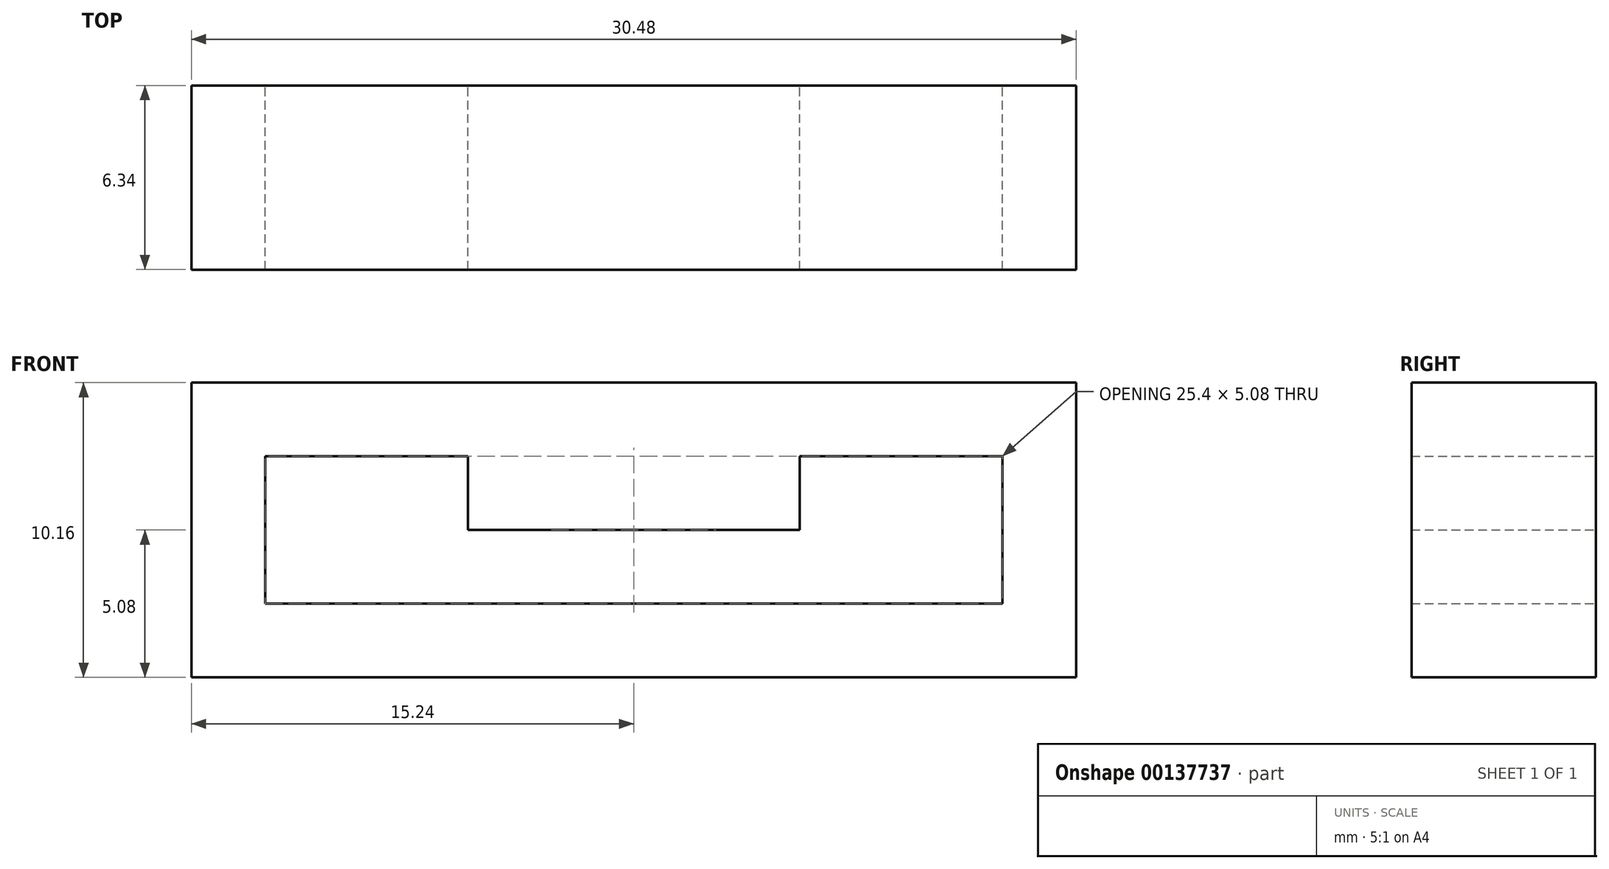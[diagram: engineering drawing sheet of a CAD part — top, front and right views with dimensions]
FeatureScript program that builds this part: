
annotation { "Feature Type Name" : "Feature", "Feature Type Description" : "" }
export const myFeature = defineFeature(function(context is Context, id is Id, definition is map)
    precondition{}
    {
        {
            var Q0;
            Q0=qCreatedBy(makeId("Front.planeOp"),FACE);
            var sketch = newSketch(context, id + "F0", { "sketchPlane" : qUnion([Q0])});
            skLineSegment(sketch, "E0.bottom", {"start": v(15.24, 5.08) * mm, "end": v(-15.24, 5.08) * mm});
            skLineSegment(sketch, "E0.top", {"start": v(15.24, -5.08) * mm, "end": v(-15.24, -5.08) * mm});
            skLineSegment(sketch, "E0.left", {"start": v(15.24, 5.08) * mm, "end": v(15.24, -5.08) * mm});
            skLineSegment(sketch, "E0.right", {"start": v(-15.24, 5.08) * mm, "end": v(-15.24, -5.08) * mm});
            skPoint(sketch, "E0.middle", {"position": v(0, 0) * mm});
            skLineSegment(sketch, "E1.bottom", {"start": v(12.7, 2.54) * mm, "end": v(-12.7, 2.54) * mm});
            skLineSegment(sketch, "E1.top", {"start": v(12.7, -2.54) * mm, "end": v(-12.7, -2.54) * mm});
            skLineSegment(sketch, "E1.left", {"start": v(12.7, 2.54) * mm, "end": v(12.7, -2.54) * mm});
            skLineSegment(sketch, "E1.right", {"start": v(-12.7, 2.54) * mm, "end": v(-12.7, -2.54) * mm});
            skLineSegment(sketch, "E2.bottom", {"start": v(-10.86, 5.08) * mm, "end": v(10.73, 5.08) * mm});
            skLineSegment(sketch, "E2.top", {"start": v(-10.86, 2.54) * mm, "end": v(10.73, 2.54) * mm});
            skLineSegment(sketch, "E2.left", {"start": v(-10.86, 5.08) * mm, "end": v(-10.86, 2.54) * mm});
            skLineSegment(sketch, "E2.right", {"start": v(10.73, 5.08) * mm, "end": v(10.73, 2.54) * mm});
            skSolve(sketch);
        }
        {
            var Q0;
            Q0 = qSketchRegion(id + "F0", true);
            extrude(context, id + "F1", {"entities" : qUnion([Q0]), "endBound" : BoundingType.SYMMETRIC, "depth" : 6.35 * mm});
        }
        {
            var Q0;
            Q0=makeQuery(id+"F1.opExtrude","SWEPT_FACE",FACE,{"disambiguationData":[OSD([sQuery(id+"F0.wireOp",EDGE,"E1.bottom"),sQuery(id+"F0.wireOp",EDGE,"E2.top")])]});
            var sketch = newSketch(context, id + "F2", { "sketchPlane" : qUnion([Q0])});
            skLineSegment(sketch, "E3.bottom", {"start": v(5.72, 3.18) * mm, "end": v(-5.72, 3.18) * mm});
            skLineSegment(sketch, "E3.top", {"start": v(5.72, -3.18) * mm, "end": v(-5.72, -3.18) * mm});
            skLineSegment(sketch, "E3.left", {"start": v(5.72, 3.18) * mm, "end": v(5.72, -3.18) * mm});
            skLineSegment(sketch, "E3.right", {"start": v(-5.72, 3.18) * mm, "end": v(-5.72, -3.18) * mm});
            skPoint(sketch, "E3.middle", {"position": v(0, 0) * mm});
            skSolve(sketch);
        }
        {
            var Q0;
            Q0=makeQuery(id+"F2.imprint","IMPRINT",FACE,{"disambiguationData":[TD([[makeQuery(id+"F2.imprint","IMPRINT",EDGE,{"derivedFrom":sQuery(id+"F2.wireOp",EDGE,"E3.bottom")}),1.0]])]});
            extrude(context, id + "F3", {"entities" : qUnion([Q0]), "operationType" : NewBodyOperationType.ADD, "depth" : 2.54 * mm});
        }
    });
